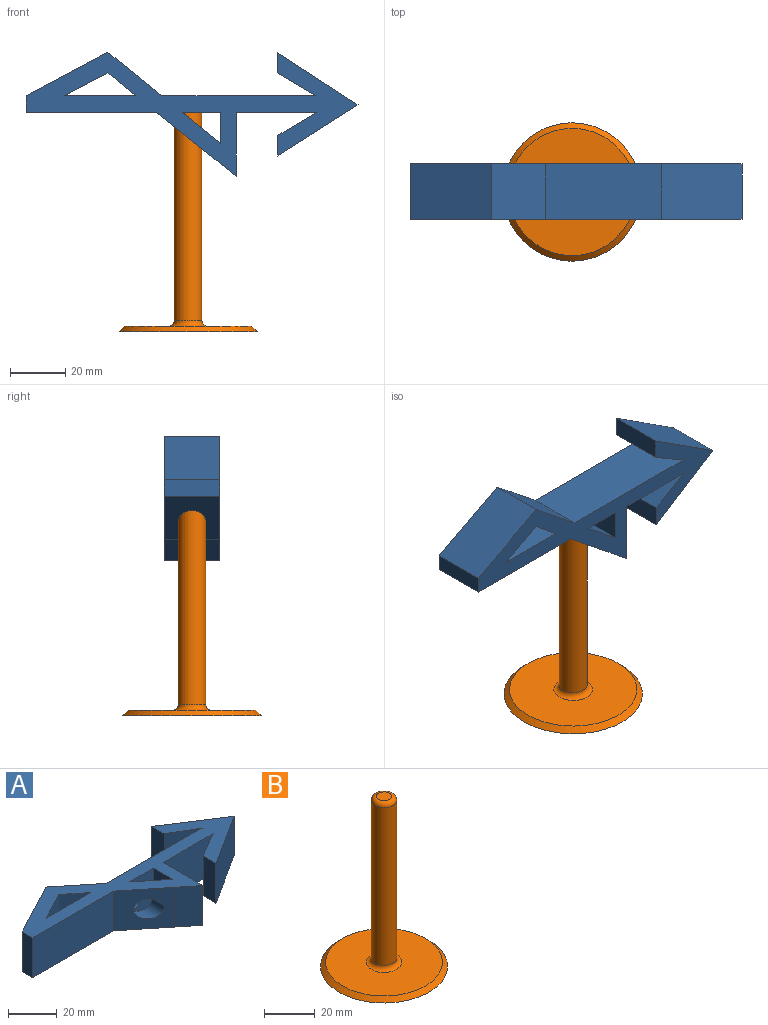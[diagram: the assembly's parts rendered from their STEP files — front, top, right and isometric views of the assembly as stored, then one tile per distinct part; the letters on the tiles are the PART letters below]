
ASSEMBLY  parts=2 mates=1
PART A: 26 faces, bbox 121.7x46.6x21.7 mm
  f0: plane 29.16x20mm, normal (0.54,0.84,0), area 694.5mm2, adj f1,f21,f22,f23
  f1: plane 20x7.29mm, normal (-1,0,0), area 145.8mm2, adj f0,f2,f22,f23
  f2: plane 20x13.9mm, normal (-0.51,-0.86,0), area 322.9mm2, adj f1,f3,f22,f23
  f3: plane 55.66x20mm, normal (0,1,0), area 1113.2mm2, adj f2,f4,f22,f23
  f4: plane 20x19.47mm, normal (0.63,0.78,0), area 500.2mm2, adj f3,f5,f22,f23
  f5: plane 29.6x20mm, normal (-0.47,0.88,0), area 670.1mm2, adj f4,f6,f22,f23
  f6: plane 20x6.05mm, normal (-1,0,0), area 121mm2, adj f5,f7,f22,f23
  f7: plane 47.25x20mm, normal (0,-1,0), area 945mm2, adj f6,f8,f22,f23
  f8: plane 21.69x21.28mm, normal (-0.63,-0.78,0), area 402.1mm2, adj f7,f9,f22,f23,f24
  f9: plane 20x9.19mm, normal (-0.63,-0.78,0), area 236.2mm2, adj f8,f10,f22,f23
  f10: plane 20x7.41mm, normal (1,0,0), area 148.1mm2, adj f9,f11,f22,f23
  f11: plane 20x15.77mm, normal (1,0,0), area 315.5mm2, adj f10,f12,f22,f23
  f12: plane 29.06x20mm, normal (0,-1,0), area 581.2mm2, adj f11,f13,f22,f23
  f13: plane 20x14.07mm, normal (-0.51,0.86,0), area 326.9mm2, adj f12,f14,f22,f23
  f14: plane 20x7.45mm, normal (-1,0,0), area 149mm2, adj f13,f21,f22,f23
  f15: plane 20x11.22mm, normal (-1,0,0), area 224.4mm2, adj f16,f19,f22,f23
  f16: plane 20.04x13.95mm, normal (0.63,0.78,0), area 281.3mm2, adj f15,f19,f22,f23,f24
  f17: plane 25.73x20mm, normal (0,1,0), area 514.5mm2, adj f18,f20,f22,f23
  f18: plane 20x15.62mm, normal (0.46,-0.89,0), area 352.8mm2, adj f17,f20,f22,f23
  f19: plane 20x13.9mm, normal (0,-1,0), area 218.7mm2, adj f15,f16,f22,f23,f24
  f20: plane 20x10.11mm, normal (-0.63,-0.78,0), area 260.3mm2, adj f17,f18,f22,f23
  f21: plane 28.95x20mm, normal (0.54,-0.84,0), area 686.9mm2, adj f0,f14,f22,f23
  f22: plane 120x44.92mm, normal (0,0,1), area 1511.9mm2, adj f0,f1,f2,f3,f4,f5,f6,f7
  f23: plane 120x44.92mm, normal (0,0,-1), area 1511.9mm2, adj f0,f1,f2,f3,f4,f5,f6,f7
  f24: cylinder r=5mm len=15.84mm, axis (0,-1,0), area 297mm2, adj f8,f16,f19,f25
  f25: plane 10x10mm, normal (0,-1,0), area 78.5mm2, adj f24
PART B: 7 faces, bbox 50x50x82 mm
  f0: plane 46x46mm, normal (0,0,1), area 1508mm2, adj f2,f5
  f1: plane 50x50mm, normal (0,0,-1), area 1963.5mm2, adj f2
  f2: cone r=23mm half-angle=45deg, axis (0,0,-1), area 426.5mm2, adj f0,f1
  f3: cylinder r=5mm len=76mm, axis (0,0,-1), area 2387.6mm2, adj f5,f6
  f4: plane 6x6mm, normal (0,0,1), area 28.3mm2, adj f6
  f5: torus R=7mm, axis (0,0,1), area 113mm2, adj f0,f3
  f6: torus R=3mm, axis (0,0,1), area 84.4mm2, adj f3,f4
PLACE A rot(axis=(1,0,0),90deg) t=(0,10,97.93)mm
PLACE B t=(0,0,15.93)mm
MATE slider B.f3 <-> A.f24  axis (0,0,1) through (0,0,97.93)mm
